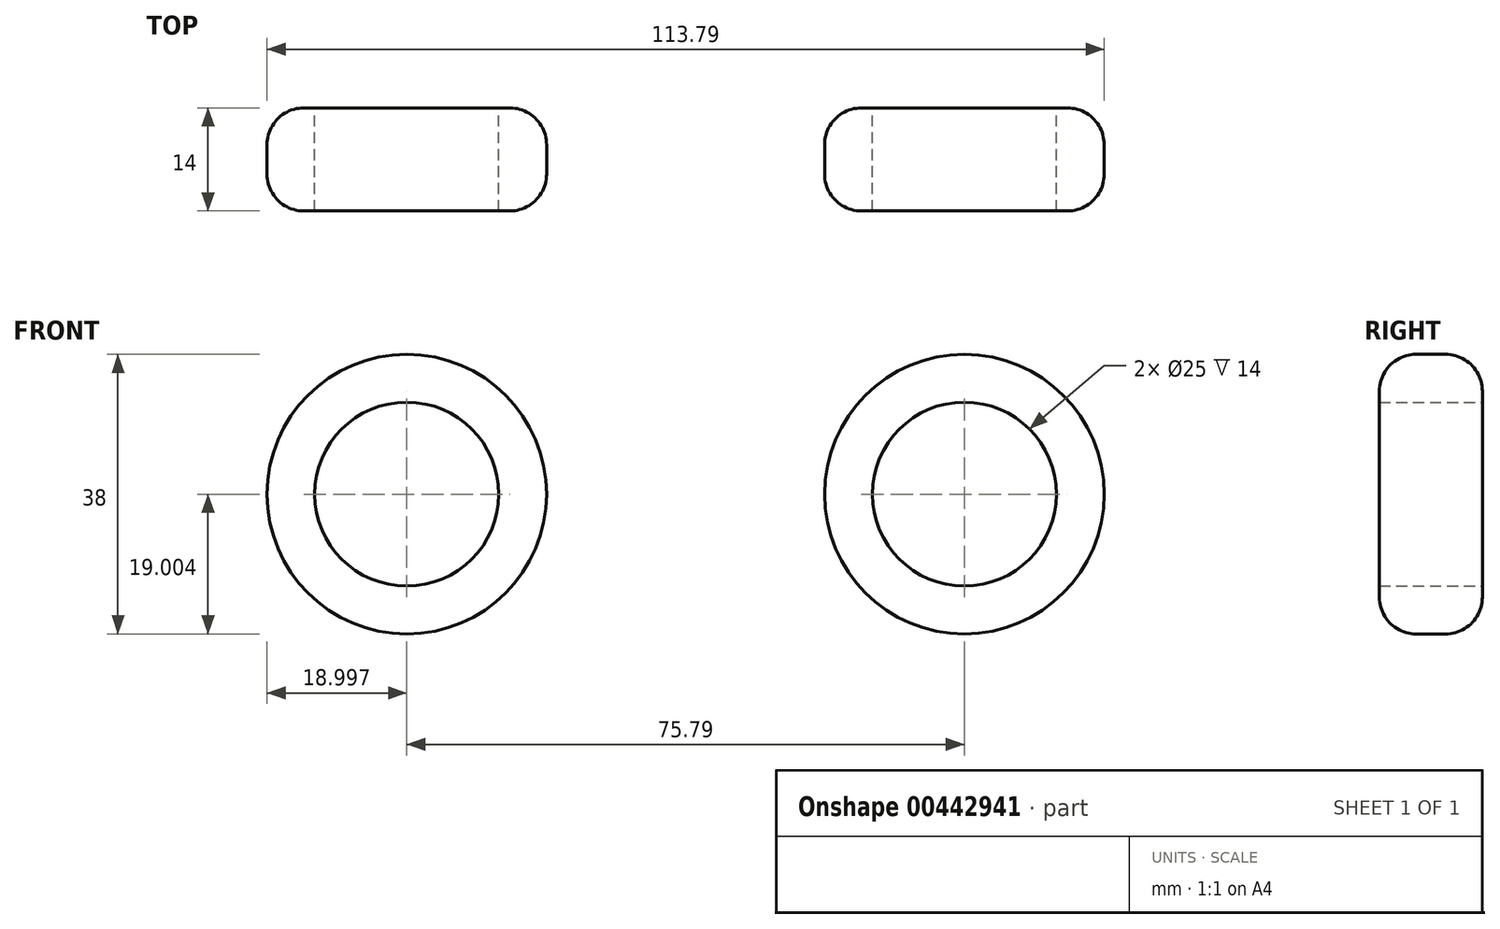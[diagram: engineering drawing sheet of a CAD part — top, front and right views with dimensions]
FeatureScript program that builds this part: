
annotation { "Feature Type Name" : "Feature", "Feature Type Description" : "" }
export const myFeature = defineFeature(function(context is Context, id is Id, definition is map)
    precondition{}
    {
        {
            var Q0;
            Q0=qCreatedBy(makeId("Front.planeOp"),FACE);
            var sketch = newSketch(context, id + "F0", { "sketchPlane" : qUnion([Q0])});
            skCircle(sketch, "E0", {"center": v(-38.78, 36.41) * mm, "radius": 19 * mm});
            skCircle(sketch, "E1", {"center": v(-38.78, 36.41) * mm, "radius": 12.5 * mm});
            skCircle(sketch, "E2", {"center": v(37, 36.41) * mm, "radius": 19 * mm});
            skCircle(sketch, "E3", {"center": v(37, 36.41) * mm, "radius": 12.5 * mm});
            skSolve(sketch);
        }
        {
            var Q0;
            Q0 = qSketchRegion(id + "F0", true);
            extrude(context, id + "F1", {"entities" : qUnion([Q0]), "depth" : 14 * mm});
        }
        {
            var Q0;
            Q0=makeQuery(id+"F1.opExtrude","SWEPT_FACE",FACE,{"disambiguationData":[OSD([sQuery(id+"F0.wireOp",EDGE,"E0")])]});
            var Q1;
            Q1=makeQuery(id+"F1.opExtrude","SWEPT_FACE",FACE,{"disambiguationData":[OSD([sQuery(id+"F0.wireOp",EDGE,"E2")])]});
            fillet(context, id + "F2", {"entities" : qUnion([Q0, Q1]), "radius" : 5 * mm, "tangentPropagation" : true, "allowEdgeOverflow" : false});
        }
    });
